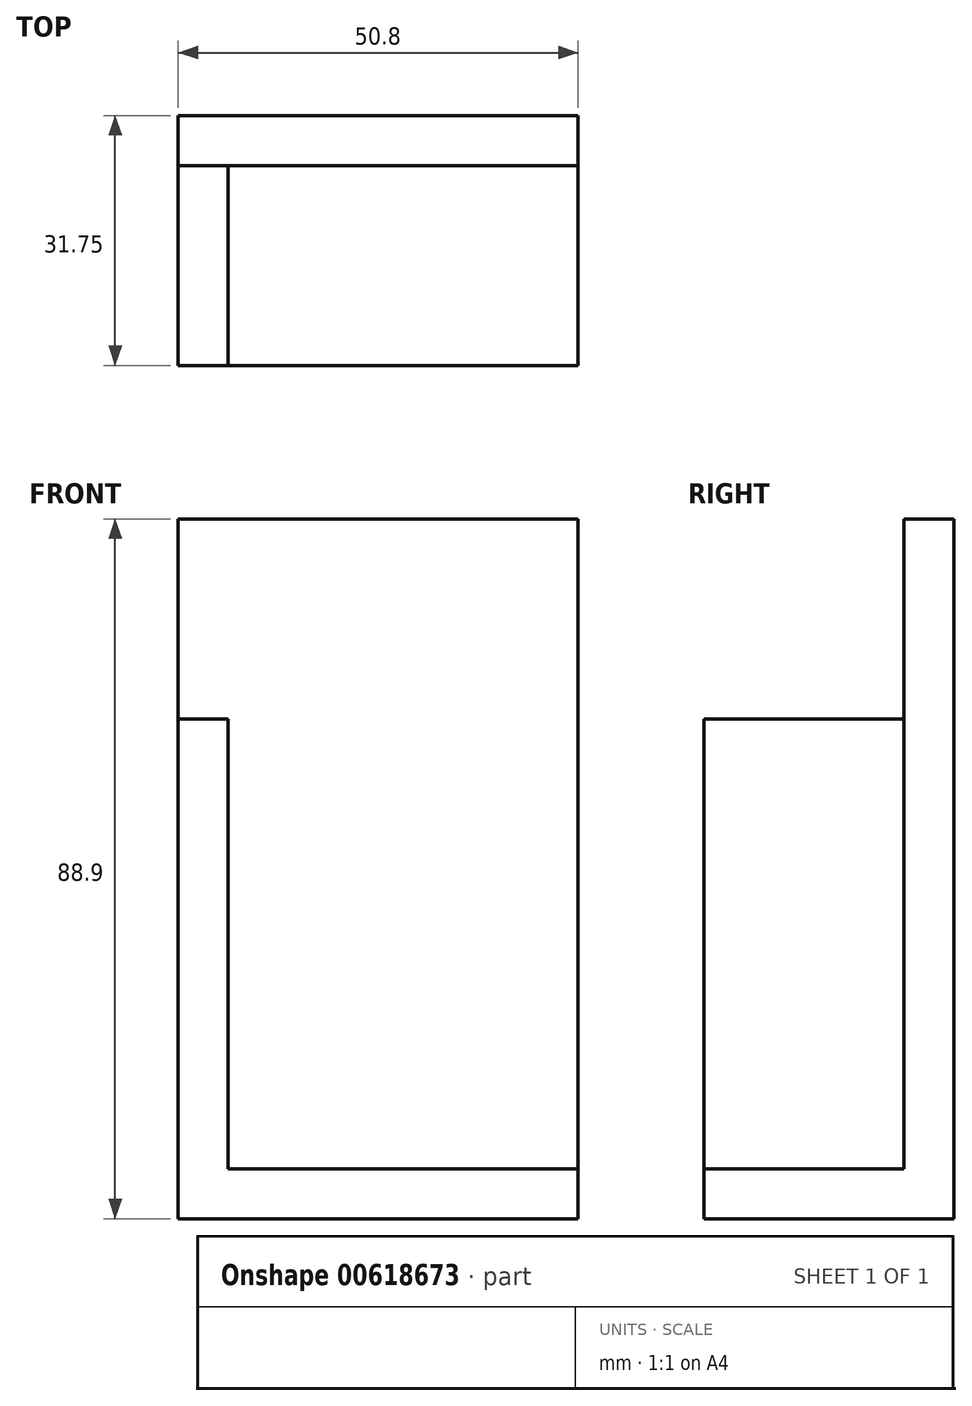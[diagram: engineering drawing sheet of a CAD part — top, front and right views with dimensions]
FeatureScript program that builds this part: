
annotation { "Feature Type Name" : "Feature", "Feature Type Description" : "" }
export const myFeature = defineFeature(function(context is Context, id is Id, definition is map)
    precondition{}
    {
        {
            var Q0;
            Q0=qCreatedBy(makeId("Front.planeOp"),FACE);
            var sketch = newSketch(context, id + "F0", { "sketchPlane" : qUnion([Q0])});
            skLineSegment(sketch, "E0.bottom", {"start": v(25.4, 44.45) * mm, "end": v(-25.4, 44.45) * mm});
            skLineSegment(sketch, "E0.top", {"start": v(25.4, -44.45) * mm, "end": v(-25.4, -44.45) * mm});
            skLineSegment(sketch, "E0.left", {"start": v(25.4, 44.45) * mm, "end": v(25.4, -44.45) * mm});
            skLineSegment(sketch, "E0.right", {"start": v(-25.4, 44.45) * mm, "end": v(-25.4, -44.45) * mm});
            skPoint(sketch, "E0.middle", {"position": v(0, 0) * mm});
            skSolve(sketch);
        }
        {
            var Q0;
            Q0=makeQuery(id+"F0.imprint","IMPRINT",FACE,{"disambiguationData":[TD([[makeQuery(id+"F0.imprint","IMPRINT",EDGE,{"derivedFrom":sQuery(id+"F0.wireOp",EDGE,"E0.bottom")}),1.0]])]});
            extrude(context, id + "F1", {"entities" : qUnion([Q0]), "depth" : 31.75 * mm, "offsetDistance" : 25.4 * mm});
        }
        {
            var Q0;
            Q0=makeQuery(id+"F1.opExtrude","SWEPT_FACE",FACE,{"disambiguationData":[OSD([sQuery(id+"F0.wireOp",EDGE,"E0.left")])]});
            var sketch = newSketch(context, id + "F2", { "sketchPlane" : qUnion([Q0])});
            skLineSegment(sketch, "E1.bottom", {"start": v(-31.75, 44.45) * mm, "end": v(-6.35, 44.45) * mm});
            skLineSegment(sketch, "E1.top", {"start": v(-31.75, -38.1) * mm, "end": v(-6.35, -38.1) * mm});
            skLineSegment(sketch, "E1.left", {"start": v(-31.75, 44.45) * mm, "end": v(-31.75, -38.1) * mm});
            skLineSegment(sketch, "E1.right", {"start": v(-6.35, 44.45) * mm, "end": v(-6.35, -38.1) * mm});
            skSolve(sketch);
        }
        {
            var Q0;
            Q0=makeQuery(id+"F2.imprint","IMPRINT",FACE,{"disambiguationData":[TD([[makeQuery(id+"F2.imprint","IMPRINT",EDGE,{"derivedFrom":sQuery(id+"F2.wireOp",EDGE,"E1.bottom")}),-1.0]])]});
            extrude(context, id + "F3", {"entities" : qUnion([Q0]), "operationType" : NewBodyOperationType.REMOVE, "oppositeDirection" : true, "depth" : 44.45 * mm, "offsetDistance" : 25.4 * mm});
        }
        {
            var Q0;
            Q0=makeQuery(id+"F1.opExtrude","SWEPT_FACE",FACE,{"disambiguationData":[OSD([sQuery(id+"F0.wireOp",EDGE,"E0.right")])]});
            var sketch = newSketch(context, id + "F4", { "sketchPlane" : qUnion([Q0])});
            skLineSegment(sketch, "E2.bottom", {"start": v(31.75, 44.45) * mm, "end": v(6.35, 44.45) * mm});
            skLineSegment(sketch, "E2.top", {"start": v(31.75, 19.05) * mm, "end": v(6.35, 19.05) * mm});
            skLineSegment(sketch, "E2.left", {"start": v(31.75, 44.45) * mm, "end": v(31.75, 19.05) * mm});
            skLineSegment(sketch, "E2.right", {"start": v(6.35, 44.45) * mm, "end": v(6.35, 19.05) * mm});
            skSolve(sketch);
        }
        {
            var Q0;
            Q0=makeQuery(id+"F4.imprint","IMPRINT",FACE,{"disambiguationData":[TD([[makeQuery(id+"F4.imprint","IMPRINT",EDGE,{"derivedFrom":sQuery(id+"F4.wireOp",EDGE,"E2.bottom")}),1.0]])]});
            extrude(context, id + "F5", {"entities" : qUnion([Q0]), "operationType" : NewBodyOperationType.REMOVE, "oppositeDirection" : true, "depth" : 25.4 * mm, "offsetDistance" : 25.4 * mm});
        }
    });
